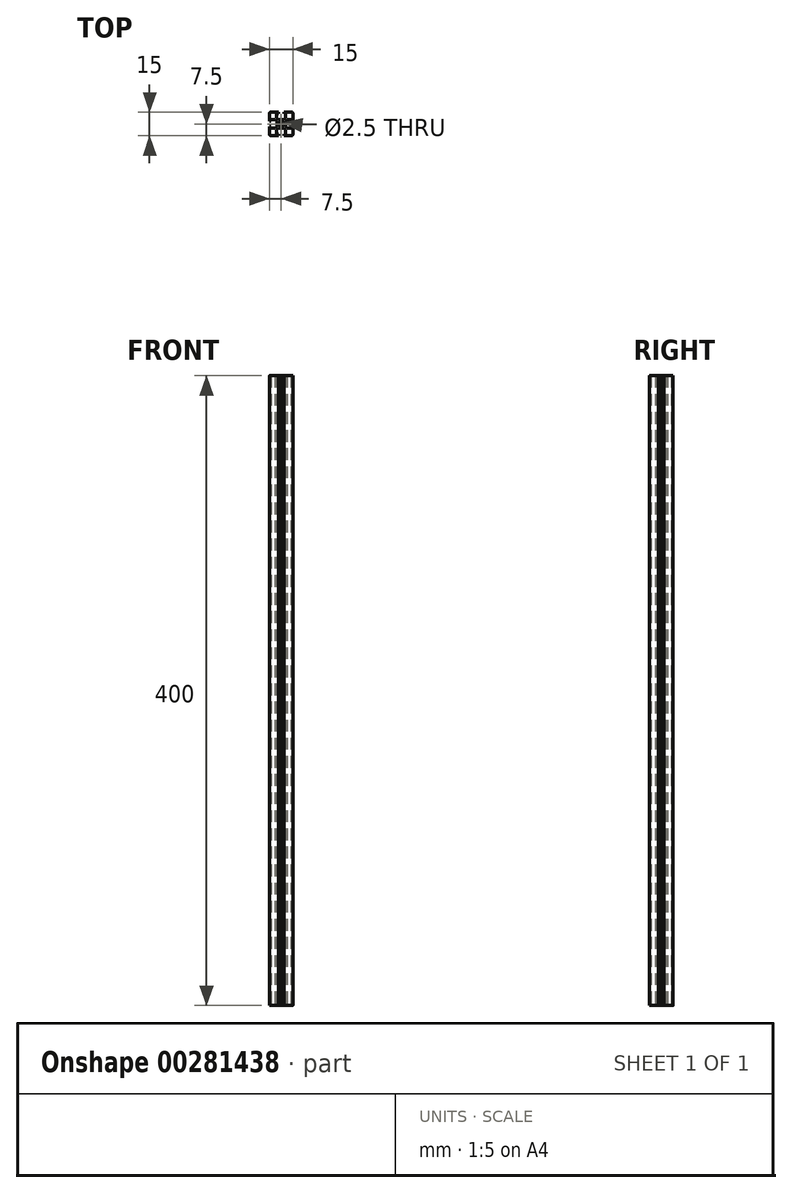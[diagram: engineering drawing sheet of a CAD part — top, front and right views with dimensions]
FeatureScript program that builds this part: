
annotation { "Feature Type Name" : "Feature", "Feature Type Description" : "" }
export const myFeature = defineFeature(function(context is Context, id is Id, definition is map)
    precondition{}
    {
        {
            var Q0;
            Q0=qCreatedBy(makeId("Top.planeOp"),FACE);
            var sketch = newSketch(context, id + "F0", { "sketchPlane" : qUnion([Q0])});
            skLineSegment(sketch, "E0.bottom", {"start": v(6.5, -7.5) * mm, "end": v(1.7, -7.5) * mm});
            skLineSegment(sketch, "E0.top", {"start": v(6.5, 7.5) * mm, "end": v(1.7, 7.5) * mm});
            skLineSegment(sketch, "E0.left", {"start": v(7.5, -6.5) * mm, "end": v(7.5, -1.7) * mm});
            skLineSegment(sketch, "E0.right", {"start": v(-7.5, -6.5) * mm, "end": v(-7.5, -1.7) * mm});
            skPoint(sketch, "E0.middle", {"position": v(0, 0) * mm});
            skPoint(sketch, "E1.visualSharp", {"position": v(7.5, 7.5) * mm});
            skArc(sketch, "E1.filletArc", {"start": v(7.5, 6.5) * mm, "mid": v(7.2, 7.2) * mm, "end": v(6.5, 7.5) * mm});
            skPoint(sketch, "E2.visualSharp", {"position": v(-7.5, 7.5) * mm});
            skArc(sketch, "E2.filletArc", {"start": v(-6.5, 7.5) * mm, "mid": v(-7.2, 7.2) * mm, "end": v(-7.5, 6.5) * mm});
            skPoint(sketch, "E3.visualSharp", {"position": v(-7.5, -7.5) * mm});
            skArc(sketch, "E3.filletArc", {"start": v(-7.5, -6.5) * mm, "mid": v(-7.2, -7.2) * mm, "end": v(-6.5, -7.5) * mm});
            skPoint(sketch, "E4.visualSharp", {"position": v(7.5, -7.5) * mm});
            skArc(sketch, "E4.filletArc", {"start": v(6.5, -7.5) * mm, "mid": v(7.2, -7.2) * mm, "end": v(7.5, -6.5) * mm});
            skCircle(sketch, "E5", {"center": v(0, 0) * mm, "radius": 1.25 * mm});
            skLineSegment(sketch, "E6", {"start": v(-1.7, 7.5) * mm, "end": v(-1.7, 6.4) * mm});
            skLineSegment(sketch, "E7", {"start": v(-1.7, 6.4) * mm, "end": v(-2.85, 6.4) * mm});
            skLineSegment(sketch, "E8", {"start": v(-2.85, 6.4) * mm, "end": v(-2.85, 3.8) * mm});
            skLineSegment(sketch, "E9", {"start": v(-2.85, 3.8) * mm, "end": v(-1.7, 2.8) * mm});
            skLineSegment(sketch, "E10", {"start": v(-1.7, 2.8) * mm, "end": v(-0.52, 2.8) * mm});
            skLineSegment(sketch, "E11", {"start": v(-0.52, 2.8) * mm, "end": v(0, 2.5) * mm});
            skLineSegment(sketch, "E12", {"start": v(0, 7.5) * mm, "end": v(0, 1.25) * mm, "construction": true});
            skLineSegment(sketch, "E13.MirrorCS", {"start": v(1.7, 7.5) * mm, "end": v(1.7, 6.4) * mm});
            skLineSegment(sketch, "E14.MirrorCS", {"start": v(1.7, 6.4) * mm, "end": v(2.85, 6.4) * mm});
            skLineSegment(sketch, "E15.MirrorCS", {"start": v(2.85, 6.4) * mm, "end": v(2.85, 3.8) * mm});
            skLineSegment(sketch, "E16.MirrorCS", {"start": v(2.85, 3.8) * mm, "end": v(1.7, 2.8) * mm});
            skLineSegment(sketch, "E17.MirrorCS", {"start": v(1.7, 2.8) * mm, "end": v(0.52, 2.8) * mm});
            skLineSegment(sketch, "E18.MirrorCS", {"start": v(0.52, 2.8) * mm, "end": v(0, 2.5) * mm});
            skLineSegment(sketch, "E19.1.0", {"start": v(-7.5, -1.7) * mm, "end": v(-6.4, -1.7) * mm});
            skLineSegment(sketch, "E19.1.1", {"start": v(-6.4, -1.7) * mm, "end": v(-6.4, -2.85) * mm});
            skLineSegment(sketch, "E19.1.2", {"start": v(-6.4, -2.85) * mm, "end": v(-3.8, -2.85) * mm});
            skLineSegment(sketch, "E19.1.3", {"start": v(-3.8, -2.85) * mm, "end": v(-2.8, -1.7) * mm});
            skLineSegment(sketch, "E19.1.4", {"start": v(-2.8, -1.7) * mm, "end": v(-2.8, -0.52) * mm});
            skLineSegment(sketch, "E19.1.5", {"start": v(-7.5, 1.7) * mm, "end": v(-6.4, 1.7) * mm});
            skLineSegment(sketch, "E19.1.6", {"start": v(-6.4, 1.7) * mm, "end": v(-6.4, 2.85) * mm});
            skLineSegment(sketch, "E19.1.7", {"start": v(-6.4, 2.85) * mm, "end": v(-3.8, 2.85) * mm});
            skLineSegment(sketch, "E19.1.8", {"start": v(-3.8, 2.85) * mm, "end": v(-2.8, 1.7) * mm});
            skLineSegment(sketch, "E19.1.9", {"start": v(-2.8, 1.7) * mm, "end": v(-2.8, 0.52) * mm});
            skLineSegment(sketch, "E19.1.10", {"start": v(-2.8, 0.52) * mm, "end": v(-2.5, 0) * mm});
            skLineSegment(sketch, "E19.1.11", {"start": v(-2.8, -0.52) * mm, "end": v(-2.5, 0) * mm});
            skLineSegment(sketch, "E19.2.0", {"start": v(1.7, -7.5) * mm, "end": v(1.7, -6.4) * mm});
            skLineSegment(sketch, "E19.2.1", {"start": v(1.7, -6.4) * mm, "end": v(2.85, -6.4) * mm});
            skLineSegment(sketch, "E19.2.2", {"start": v(2.85, -6.4) * mm, "end": v(2.85, -3.8) * mm});
            skLineSegment(sketch, "E19.2.3", {"start": v(2.85, -3.8) * mm, "end": v(1.7, -2.8) * mm});
            skLineSegment(sketch, "E19.2.4", {"start": v(1.7, -2.8) * mm, "end": v(0.52, -2.8) * mm});
            skLineSegment(sketch, "E19.2.5", {"start": v(-1.7, -7.5) * mm, "end": v(-1.7, -6.4) * mm});
            skLineSegment(sketch, "E19.2.6", {"start": v(-1.7, -6.4) * mm, "end": v(-2.85, -6.4) * mm});
            skLineSegment(sketch, "E19.2.7", {"start": v(-2.85, -6.4) * mm, "end": v(-2.85, -3.8) * mm});
            skLineSegment(sketch, "E19.2.8", {"start": v(-2.85, -3.8) * mm, "end": v(-1.7, -2.8) * mm});
            skLineSegment(sketch, "E19.2.9", {"start": v(-1.7, -2.8) * mm, "end": v(-0.52, -2.8) * mm});
            skLineSegment(sketch, "E19.2.10", {"start": v(-0.52, -2.8) * mm, "end": v(0, -2.5) * mm});
            skLineSegment(sketch, "E19.2.11", {"start": v(0.52, -2.8) * mm, "end": v(0, -2.5) * mm});
            skLineSegment(sketch, "E19.3.0", {"start": v(7.5, 1.7) * mm, "end": v(6.4, 1.7) * mm});
            skLineSegment(sketch, "E19.3.1", {"start": v(6.4, 1.7) * mm, "end": v(6.4, 2.85) * mm});
            skLineSegment(sketch, "E19.3.2", {"start": v(6.4, 2.85) * mm, "end": v(3.8, 2.85) * mm});
            skLineSegment(sketch, "E19.3.3", {"start": v(3.8, 2.85) * mm, "end": v(2.8, 1.7) * mm});
            skLineSegment(sketch, "E19.3.4", {"start": v(2.8, 1.7) * mm, "end": v(2.8, 0.52) * mm});
            skLineSegment(sketch, "E19.3.5", {"start": v(7.5, -1.7) * mm, "end": v(6.4, -1.7) * mm});
            skLineSegment(sketch, "E19.3.6", {"start": v(6.4, -1.7) * mm, "end": v(6.4, -2.85) * mm});
            skLineSegment(sketch, "E19.3.7", {"start": v(6.4, -2.85) * mm, "end": v(3.8, -2.85) * mm});
            skLineSegment(sketch, "E19.3.8", {"start": v(3.8, -2.85) * mm, "end": v(2.8, -1.7) * mm});
            skLineSegment(sketch, "E19.3.9", {"start": v(2.8, -1.7) * mm, "end": v(2.8, -0.52) * mm});
            skLineSegment(sketch, "E19.3.10", {"start": v(2.8, -0.52) * mm, "end": v(2.5, 0) * mm});
            skLineSegment(sketch, "E19.3.11", {"start": v(2.8, 0.52) * mm, "end": v(2.5, 0) * mm});
            skLineSegment(sketch, "E20.trimOffspring", {"start": v(-7.5, 1.7) * mm, "end": v(-7.5, 6.5) * mm});
            skLineSegment(sketch, "E21.trimOffspring", {"start": v(-1.7, -7.5) * mm, "end": v(-6.5, -7.5) * mm});
            skLineSegment(sketch, "E22.trimOffspring", {"start": v(7.5, 1.7) * mm, "end": v(7.5, 6.5) * mm});
            skLineSegment(sketch, "E23.trimOffspring", {"start": v(-1.7, 7.5) * mm, "end": v(-6.5, 7.5) * mm});
            skSolve(sketch);
        }
        {
            var Q0;
            Q0=qSketchRegion(id+"F0",true);
            extrude(context, id + "F1", {"entities" : qUnion([Q0]), "endBound" : BoundingType.SYMMETRIC, "depth" : 400 * mm});
        }
    });
